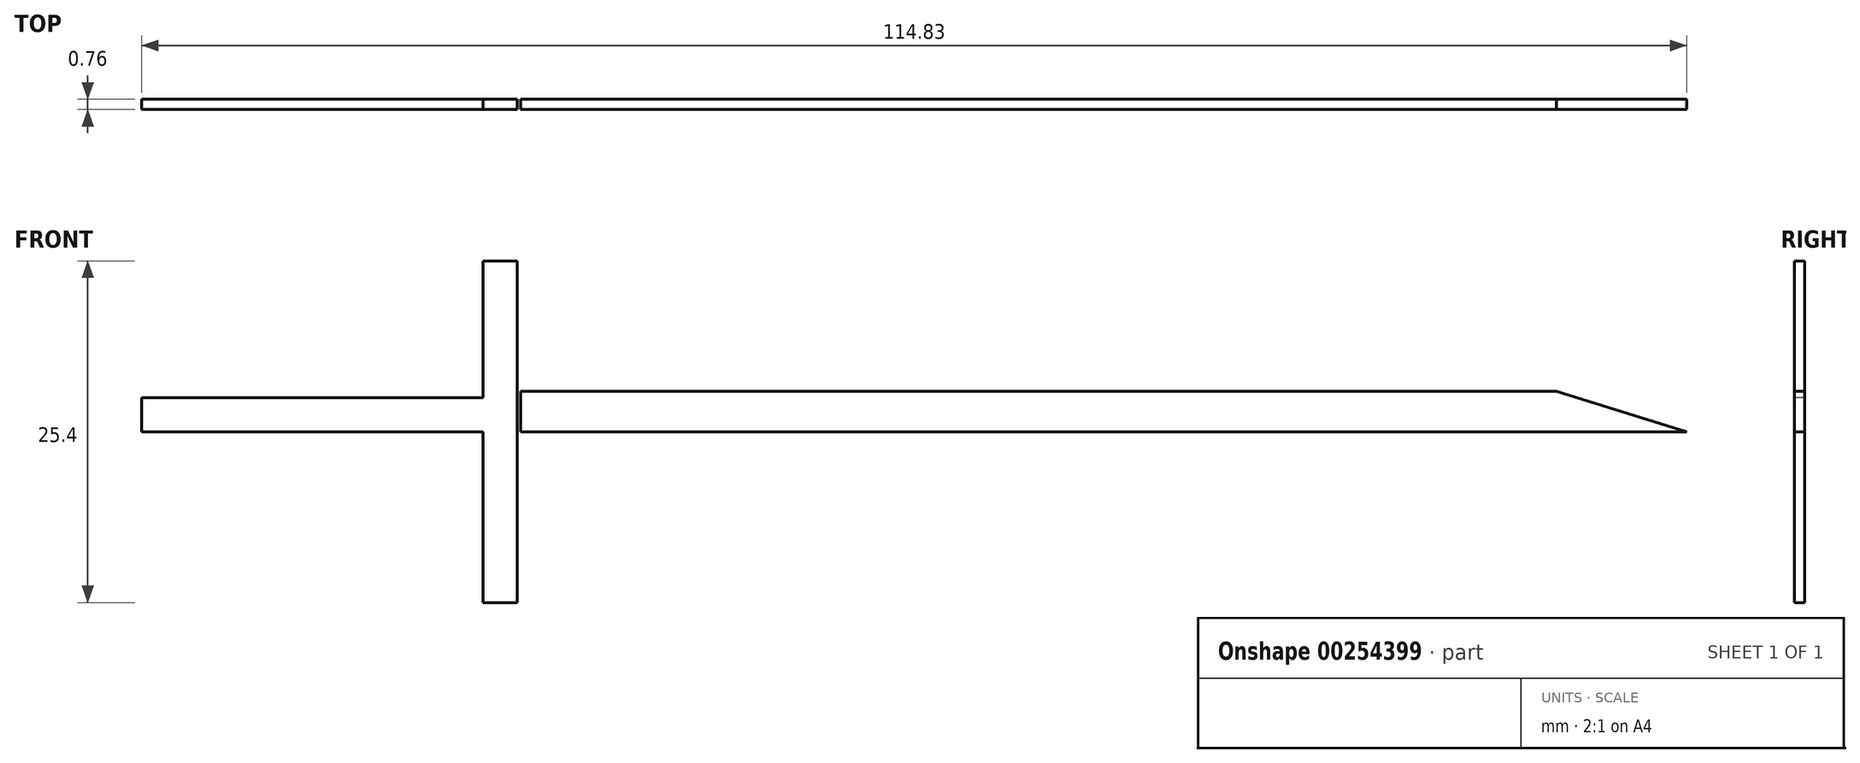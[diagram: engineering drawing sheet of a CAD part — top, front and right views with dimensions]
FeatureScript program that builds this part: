
annotation { "Feature Type Name" : "Feature", "Feature Type Description" : "" }
export const myFeature = defineFeature(function(context is Context, id is Id, definition is map)
    precondition{}
    {
        {
            var Q0;
            Q0=qCreatedBy(makeId("Front.planeOp"),FACE);
            var sketch = newSketch(context, id + "F0", { "sketchPlane" : qUnion([Q0])});
            skLineSegment(sketch, "E0", {"start": v(-69.64, 0) * mm, "end": v(-44.24, 0) * mm});
            skLineSegment(sketch, "E1", {"start": v(-44.24, 0) * mm, "end": v(-44.24, 2.54) * mm});
            skLineSegment(sketch, "E2", {"start": v(-44.24, 2.54) * mm, "end": v(-69.64, 2.54) * mm});
            skLineSegment(sketch, "E3", {"start": v(-69.64, 2.54) * mm, "end": v(-69.64, 0) * mm});
            skSolve(sketch);
        }
        {
            var Q0;
            Q0=qCreatedBy(makeId("Front.planeOp"),FACE);
            var sketch = newSketch(context, id + "F1", { "sketchPlane" : qUnion([Q0])});
            skLineSegment(sketch, "E4", {"start": v(-44.26, 0) * mm, "end": v(-44.26, -12.7) * mm});
            skLineSegment(sketch, "E5", {"start": v(-44.26, 0) * mm, "end": v(-44.26, 12.7) * mm});
            skLineSegment(sketch, "E6", {"start": v(-44.26, 12.7) * mm, "end": v(-41.72, 12.7) * mm});
            skLineSegment(sketch, "E7", {"start": v(-41.72, 12.7) * mm, "end": v(-41.72, -12.7) * mm});
            skLineSegment(sketch, "E8", {"start": v(-44.26, -12.7) * mm, "end": v(-41.72, -12.7) * mm});
            skPoint(sketch, "E9.start.orphan", {"position": v(-41.72, 0) * mm});
            skSolve(sketch);
        }
        {
            var Q0;
            Q0=qCreatedBy(makeId("Front.planeOp"),FACE);
            var sketch = newSketch(context, id + "F2", { "sketchPlane" : qUnion([Q0])});
            skLineSegment(sketch, "E10", {"start": v(-41.48, 0) * mm, "end": v(34.72, 0) * mm});
            skLineSegment(sketch, "E11", {"start": v(35.49, 3.01) * mm, "end": v(45.19, 0) * mm});
            skLineSegment(sketch, "E12", {"start": v(45.19, 0) * mm, "end": v(34.72, 0) * mm});
            skLineSegment(sketch, "E13", {"start": v(35.49, 3.01) * mm, "end": v(-41.48, 3.01) * mm});
            skLineSegment(sketch, "E14", {"start": v(-41.48, 3.01) * mm, "end": v(-41.48, 0) * mm});
            skSolve(sketch);
        }
        {
            var Q0;
            Q0=makeQuery(id+"F2.imprint","IMPRINT",FACE,{"disambiguationData":[TD([[makeQuery(id+"F2.imprint","IMPRINT",EDGE,{"derivedFrom":sQuery(id+"F2.wireOp",EDGE,"E10")}),1.0]])]});
            extrude(context, id + "F3", {"entities" : qUnion([Q0]), "depth" : 0.76 * mm});
        }
        {
            var Q0;
            Q0=makeQuery(id+"F1.imprint","IMPRINT",FACE,{"disambiguationData":[TD([[makeQuery(id+"F1.imprint","IMPRINT",EDGE,{"derivedFrom":sQuery(id+"F1.wireOp",EDGE,"E4")}),1.0]])]});
            extrude(context, id + "F4", {"entities" : qUnion([Q0]), "depth" : 0.76 * mm});
        }
        {
            var Q0;
            Q0=makeQuery(id+"F0.imprint","IMPRINT",FACE,{"disambiguationData":[TD([[makeQuery(id+"F0.imprint","IMPRINT",EDGE,{"derivedFrom":sQuery(id+"F0.wireOp",EDGE,"E0")}),1.0]])]});
            extrude(context, id + "F5", {"entities" : qUnion([Q0]), "operationType" : NewBodyOperationType.ADD, "depth" : 0.76 * mm});
        }
    });
